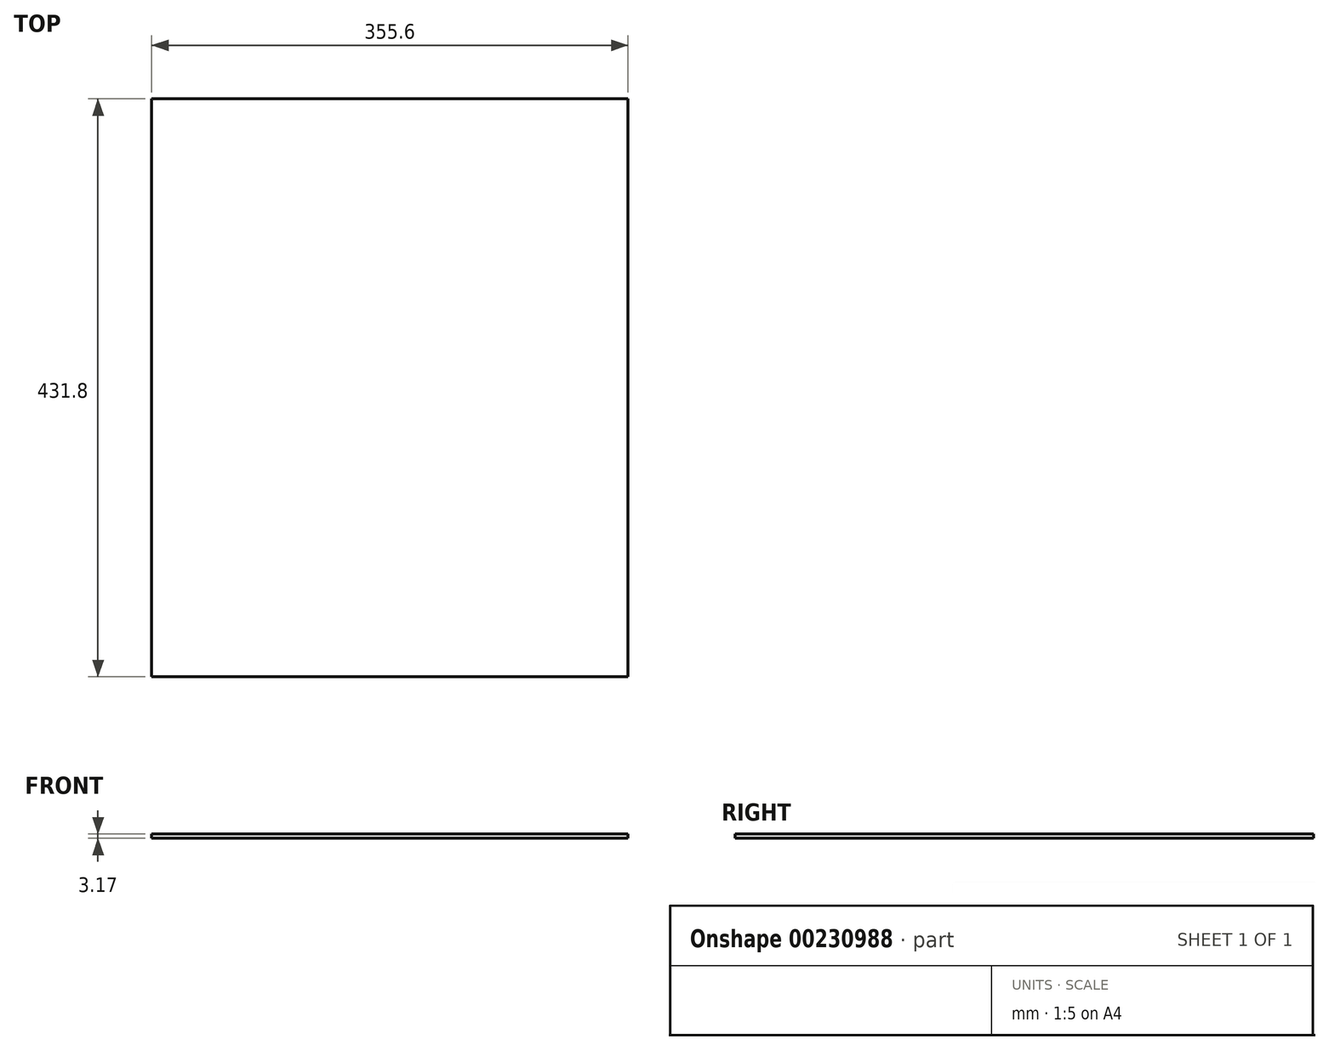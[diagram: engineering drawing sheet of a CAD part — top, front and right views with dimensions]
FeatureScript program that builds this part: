
annotation { "Feature Type Name" : "Feature", "Feature Type Description" : "" }
export const myFeature = defineFeature(function(context is Context, id is Id, definition is map)
    precondition{}
    {
        {
            var Q0;
            Q0=qCreatedBy(makeId("Top.planeOp"),FACE);
            var sketch = newSketch(context, id + "F0", { "sketchPlane" : qUnion([Q0])});
            skLineSegment(sketch, "E0.bottom", {"start": v(0, 0) * mm, "end": v(355.6, 0) * mm});
            skLineSegment(sketch, "E0.top", {"start": v(0, 431.8) * mm, "end": v(355.6, 431.8) * mm});
            skLineSegment(sketch, "E0.left", {"start": v(0, 0) * mm, "end": v(0, 431.8) * mm});
            skLineSegment(sketch, "E0.right", {"start": v(355.6, 0) * mm, "end": v(355.6, 431.8) * mm});
            skSolve(sketch);
        }
        {
            var Q0;
            Q0 = qSketchRegion(id + "F0", true);
            extrude(context, id + "F1", {"entities" : qUnion([Q0]), "depth" : 3.17 * mm});
        }
    });
